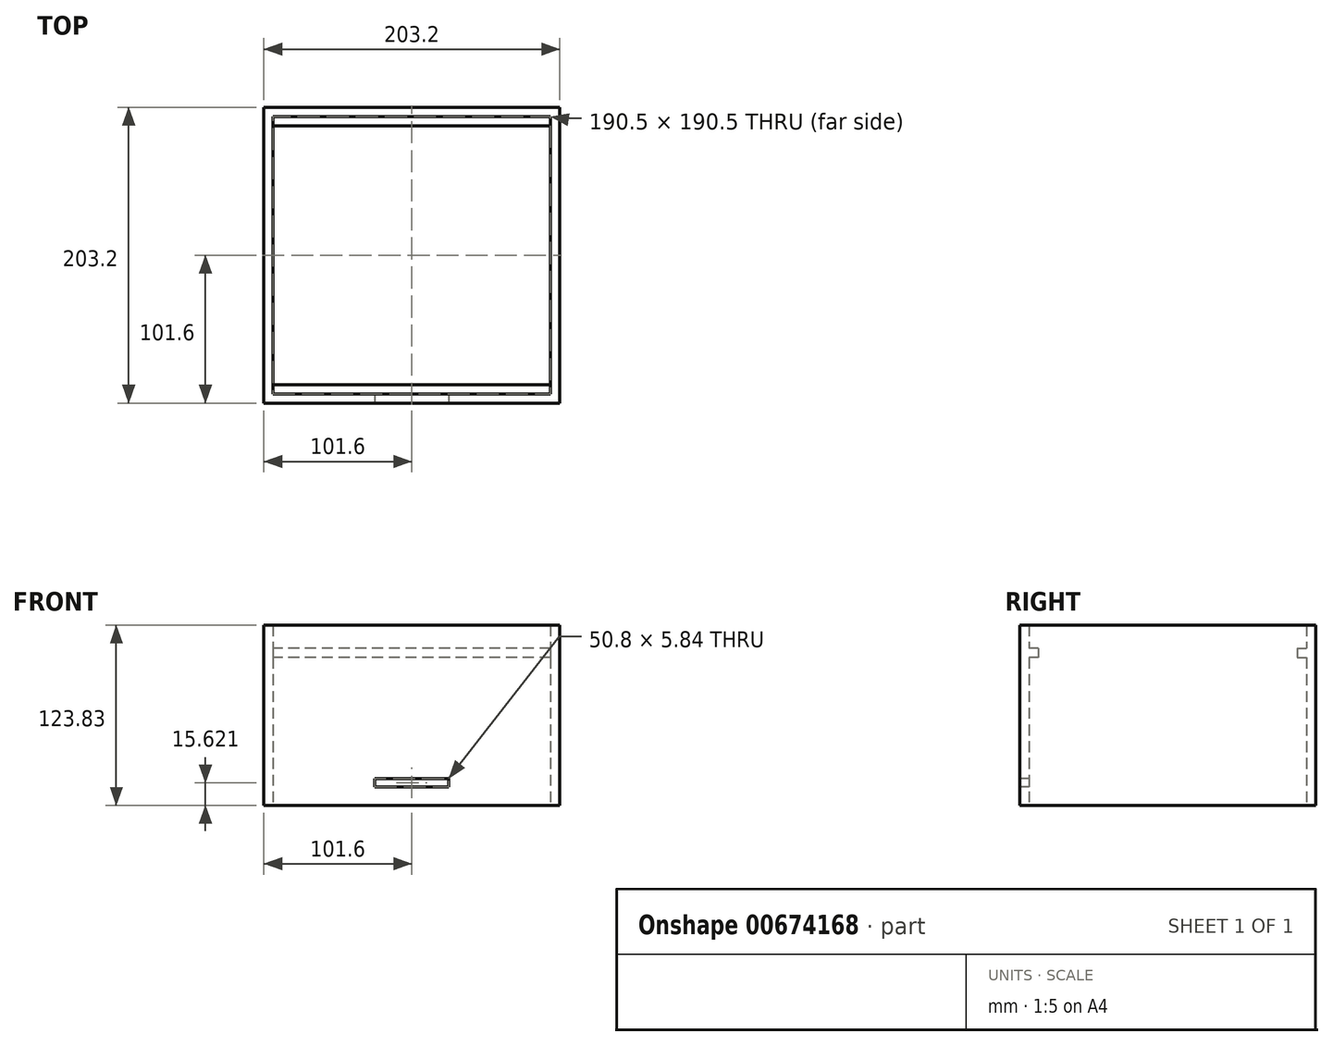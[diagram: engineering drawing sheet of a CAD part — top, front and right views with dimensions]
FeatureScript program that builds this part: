
annotation { "Feature Type Name" : "Feature", "Feature Type Description" : "" }
export const myFeature = defineFeature(function(context is Context, id is Id, definition is map)
    precondition{}
    {
        {
            var Q0;
            Q0=qCreatedBy(makeId("Top.planeOp"),FACE);
            var sketch = newSketch(context, id + "F0", { "sketchPlane" : qUnion([Q0])});
            skLineSegment(sketch, "E0.bottom", {"start": v(-101.6, 101.6) * mm, "end": v(101.6, 101.6) * mm});
            skLineSegment(sketch, "E0.top", {"start": v(-101.6, -101.6) * mm, "end": v(101.6, -101.6) * mm});
            skLineSegment(sketch, "E0.left", {"start": v(-101.6, 101.6) * mm, "end": v(-101.6, -101.6) * mm});
            skLineSegment(sketch, "E0.right", {"start": v(101.6, 101.6) * mm, "end": v(101.6, -101.6) * mm});
            skPoint(sketch, "E0.middle", {"position": v(0, 0) * mm});
            skLineSegment(sketch, "E1.bottom", {"start": v(-95.25, 95.25) * mm, "end": v(95.25, 95.25) * mm});
            skLineSegment(sketch, "E1.top", {"start": v(-95.25, -95.25) * mm, "end": v(95.25, -95.25) * mm});
            skLineSegment(sketch, "E1.left", {"start": v(-95.25, 95.25) * mm, "end": v(-95.25, -95.25) * mm});
            skLineSegment(sketch, "E1.right", {"start": v(95.25, 95.25) * mm, "end": v(95.25, -95.25) * mm});
            skLineSegment(sketch, "E2", {"start": v(-95.25, 95.25) * mm, "end": v(-101.6, 101.6) * mm});
            skLineSegment(sketch, "E3", {"start": v(95.25, 95.25) * mm, "end": v(101.6, 101.6) * mm});
            skLineSegment(sketch, "E4", {"start": v(101.6, -101.6) * mm, "end": v(95.25, -95.25) * mm});
            skLineSegment(sketch, "E5", {"start": v(-95.25, -95.25) * mm, "end": v(-101.6, -101.6) * mm});
            skSolve(sketch);
        }
        {
            var Q0;
            Q0=makeQuery(id+"F0.imprint","IMPRINT",FACE,{"disambiguationData":[TD([[makeQuery(id+"F0.imprint","IMPRINT",EDGE,{"derivedFrom":sQuery(id+"F0.wireOp",EDGE,"E0.right")}),-1.0]])]});
            var Q1;
            Q1=makeQuery(id+"F0.imprint","IMPRINT",FACE,{"disambiguationData":[TD([[makeQuery(id+"F0.imprint","IMPRINT",EDGE,{"derivedFrom":sQuery(id+"F0.wireOp",EDGE,"E0.top")}),1.0]])]});
            var Q2;
            Q2=makeQuery(id+"F0.imprint","IMPRINT",FACE,{"disambiguationData":[TD([[makeQuery(id+"F0.imprint","IMPRINT",EDGE,{"derivedFrom":sQuery(id+"F0.wireOp",EDGE,"E0.left")}),1.0]])]});
            var Q3;
            Q3=makeQuery(id+"F0.imprint","IMPRINT",FACE,{"disambiguationData":[TD([[makeQuery(id+"F0.imprint","IMPRINT",EDGE,{"derivedFrom":sQuery(id+"F0.wireOp",EDGE,"E0.bottom")}),-1.0]])]});
            extrude(context, id + "F1", {"entities" : qUnion([Q0, Q1, Q2, Q3]), "depth" : 123.82 * mm, "offsetDistance" : 25.4 * mm});
        }
        {
            var Q0;
            Q0=makeQuery(id+"F1.opExtrude","SWEPT_FACE",FACE,{"disambiguationData":[OSD([sQuery(id+"F0.wireOp",EDGE,"E1.bottom")])]});
            var sketch = newSketch(context, id + "F2", { "sketchPlane" : qUnion([Q0])});
            skLineSegment(sketch, "E6.bottom", {"start": v(95.25, 107.95) * mm, "end": v(-95.25, 107.95) * mm});
            skLineSegment(sketch, "E6.top", {"start": v(95.25, 101.6) * mm, "end": v(-95.25, 101.6) * mm});
            skLineSegment(sketch, "E6.left", {"start": v(95.25, 107.95) * mm, "end": v(95.25, 101.6) * mm});
            skLineSegment(sketch, "E6.right", {"start": v(-95.25, 107.95) * mm, "end": v(-95.25, 101.6) * mm});
            skSolve(sketch);
        }
        {
            var Q0;
            Q0 = qSketchRegion(id + "F2", true);
            extrude(context, id + "F3", {"entities" : qUnion([Q0]), "operationType" : NewBodyOperationType.ADD, "depth" : 6.35 * mm, "offsetDistance" : 25.4 * mm});
        }
        {
            var Q0;
            Q0=makeQuery(id+"F1.opExtrude","SWEPT_FACE",FACE,{"disambiguationData":[OSD([sQuery(id+"F0.wireOp",EDGE,"E1.top")])]});
            var sketch = newSketch(context, id + "F4", { "sketchPlane" : qUnion([Q0])});
            skLineSegment(sketch, "E7.bottom", {"start": v(-95.25, 107.95) * mm, "end": v(95.25, 107.95) * mm});
            skLineSegment(sketch, "E7.top", {"start": v(-95.25, 101.6) * mm, "end": v(95.25, 101.6) * mm});
            skLineSegment(sketch, "E7.left", {"start": v(-95.25, 107.95) * mm, "end": v(-95.25, 101.6) * mm});
            skLineSegment(sketch, "E7.right", {"start": v(95.25, 107.95) * mm, "end": v(95.25, 101.6) * mm});
            skSolve(sketch);
        }
        {
            var Q0;
            Q0 = qSketchRegion(id + "F4", true);
            extrude(context, id + "F5", {"entities" : qUnion([Q0]), "operationType" : NewBodyOperationType.ADD, "depth" : 6.35 * mm, "offsetDistance" : 25.4 * mm});
        }
        {
            var Q0;
            Q0=makeQuery(id+"F1.opExtrude","SWEPT_FACE",FACE,{"disambiguationData":[OSD([sQuery(id+"F0.wireOp",EDGE,"E0.top")])]});
            var sketch = newSketch(context, id + "F6", { "sketchPlane" : qUnion([Q0])});
            skLineSegment(sketch, "E8", {"start": v(0, 0) * mm, "end": v(0, 12.7) * mm});
            skLineSegment(sketch, "E9", {"start": v(0, 12.7) * mm, "end": v(25.4, 12.7) * mm});
            skLineSegment(sketch, "E10", {"start": v(25.4, 12.7) * mm, "end": v(25.4, 18.54) * mm});
            skLineSegment(sketch, "E11", {"start": v(25.4, 18.54) * mm, "end": v(-25.4, 18.54) * mm});
            skLineSegment(sketch, "E12", {"start": v(-25.4, 18.54) * mm, "end": v(-25.4, 12.7) * mm});
            skLineSegment(sketch, "E13", {"start": v(-25.4, 12.7) * mm, "end": v(0, 12.7) * mm});
            skSolve(sketch);
        }
        {
            var Q0;
            Q0 = qSketchRegion(id + "F6", true);
            extrude(context, id + "F7", {"entities" : qUnion([Q0]), "operationType" : NewBodyOperationType.REMOVE, "oppositeDirection" : true, "depth" : 25.4 * mm, "offsetDistance" : 25.4 * mm});
        }
    });
